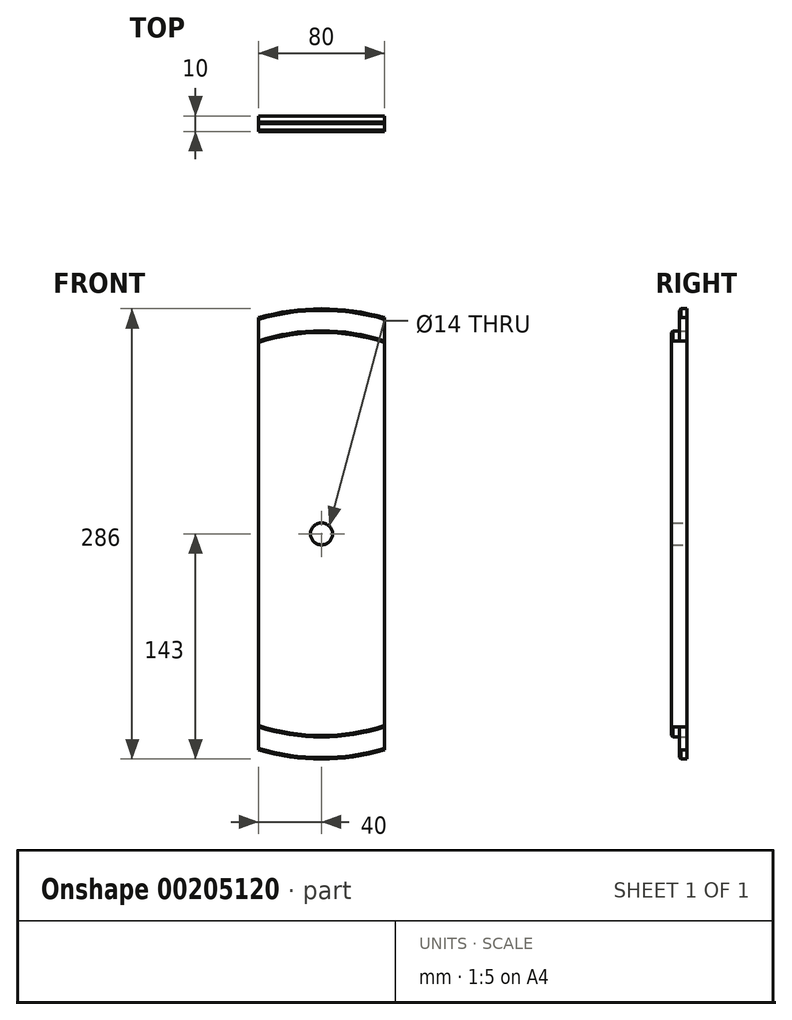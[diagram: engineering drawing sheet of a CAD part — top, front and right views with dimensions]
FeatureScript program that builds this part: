
annotation { "Feature Type Name" : "Feature", "Feature Type Description" : "" }
export const myFeature = defineFeature(function(context is Context, id is Id, definition is map)
    precondition{}
    {
        {
            var Q0;
            Q0=qCreatedBy(makeId("Front.planeOp"),FACE);
            var sketch = newSketch(context, id + "F0", { "sketchPlane" : qUnion([Q0])});
            skCircle(sketch, "E0", {"center": v(0, 0) * mm, "radius": 143 * mm});
            skCircle(sketch, "E1", {"center": v(0, 0) * mm, "radius": 129 * mm});
            skCircle(sketch, "E2", {"center": v(0, 0) * mm, "radius": 7 * mm});
            skLineSegment(sketch, "E3.bottom", {"start": v(-40, 146.77) * mm, "end": v(40, 146.77) * mm});
            skLineSegment(sketch, "E3.top", {"start": v(-40, -149.83) * mm, "end": v(40, -149.83) * mm});
            skLineSegment(sketch, "E3.left", {"start": v(-40, 146.77) * mm, "end": v(-40, -149.83) * mm});
            skLineSegment(sketch, "E3.right", {"start": v(40, 146.77) * mm, "end": v(40, -149.83) * mm});
            skSolve(sketch);
        }
        {
            var Q0;
            {var subQ0=sQuery(id+"F0.wireOp",EDGE,"E3.left");var subQ1=sQuery(id+"F0.wireOp",EDGE,"E0");var subQ2=makeQuery(id+"F0.imprint","INTERSECT",VERTEX,{"disambiguationData":[OD(1.0)],"derivedFrom":[subQ1,subQ0]});Q0=makeQuery(id+"F0.imprint","IMPRINT",FACE,{"disambiguationData":[TD([[makeQuery(id+"F0.imprint","IMPRINT",EDGE,{"disambiguationData":[TD([[subQ2,-1.0]])],"derivedFrom":subQ1}),1.0]])]});}
            var Q1;
            {var subQ0=sQuery(id+"F0.wireOp",EDGE,"E3.left");var subQ1=sQuery(id+"F0.wireOp",EDGE,"E0");var subQ2=makeQuery(id+"F0.imprint","INTERSECT",VERTEX,{"disambiguationData":[OD(0.0)],"derivedFrom":[subQ1,subQ0]});Q1=makeQuery(id+"F0.imprint","IMPRINT",FACE,{"disambiguationData":[TD([[makeQuery(id+"F0.imprint","IMPRINT",EDGE,{"disambiguationData":[TD([[subQ2,1.0]])],"derivedFrom":subQ1}),1.0]])]});}
            extrude(context, id + "F1", {"entities" : qUnion([Q0, Q1]), "depth" : 5 * mm});
        }
        {
            var Q0;
            Q0=makeQuery(id+"F0.imprint","IMPRINT",FACE,{"disambiguationData":[TD([[makeQuery(id+"F0.imprint","IMPRINT",EDGE,{"derivedFrom":sQuery(id+"F0.wireOp",EDGE,"E2")}),-1.0]])]});
            extrude(context, id + "F2", {"entities" : qUnion([Q0]), "depth" : 10 * mm});
        }
        {
            var Q0;
            {var subQ0=sQuery(id+"F0.wireOp",EDGE,"E0");Q0=makeQuery(id+"F1.opExtrude","CAP_EDGE",EDGE,{"disambiguationData":[OSD([subQ0]),TDD([makeQuery(id+"F0.imprint","IMPRINT",EDGE,{"disambiguationData":[TD([[makeQuery(id+"F0.imprint","INTERSECT",VERTEX,{"disambiguationData":[OD(1.0)],"derivedFrom":[subQ0,sQuery(id+"F0.wireOp",EDGE,"E3.left")]}),-1.0]])],"derivedFrom":subQ0})])],"isStart":false});}
            var Q1;
            {var subQ0=sQuery(id+"F0.wireOp",EDGE,"E1");Q1=makeQuery(id+"F2.opExtrude","CAP_EDGE",EDGE,{"disambiguationData":[OSD([subQ0]),TDD([makeQuery(id+"F0.imprint","IMPRINT",EDGE,{"disambiguationData":[TD([[makeQuery(id+"F0.imprint","INTERSECT",VERTEX,{"disambiguationData":[OD(1.0)],"derivedFrom":[subQ0,sQuery(id+"F0.wireOp",EDGE,"E3.left")]}),-1.0]])],"derivedFrom":subQ0})])],"isStart":false});}
            var Q2;
            {var subQ0=sQuery(id+"F0.wireOp",EDGE,"E0");Q2=makeQuery(id+"F1.opExtrude","CAP_EDGE",EDGE,{"disambiguationData":[OSD([subQ0]),TDD([makeQuery(id+"F0.imprint","IMPRINT",EDGE,{"disambiguationData":[TD([[makeQuery(id+"F0.imprint","INTERSECT",VERTEX,{"disambiguationData":[OD(0.0)],"derivedFrom":[subQ0,sQuery(id+"F0.wireOp",EDGE,"E3.left")]}),1.0]])],"derivedFrom":subQ0})])],"isStart":false});}
            var Q3;
            {var subQ0=sQuery(id+"F0.wireOp",EDGE,"E1");Q3=makeQuery(id+"F2.opExtrude","CAP_EDGE",EDGE,{"disambiguationData":[OSD([subQ0]),TDD([makeQuery(id+"F0.imprint","IMPRINT",EDGE,{"disambiguationData":[TD([[makeQuery(id+"F0.imprint","INTERSECT",VERTEX,{"disambiguationData":[OD(0.0)],"derivedFrom":[subQ0,sQuery(id+"F0.wireOp",EDGE,"E3.left")]}),1.0]])],"derivedFrom":subQ0})])],"isStart":false});}
            chamfer(context, id + "F3", {"entities" : qUnion([Q0, Q1, Q2, Q3]), "width" : 1 * mm, "tangentPropagation" : true});
        }
    });
